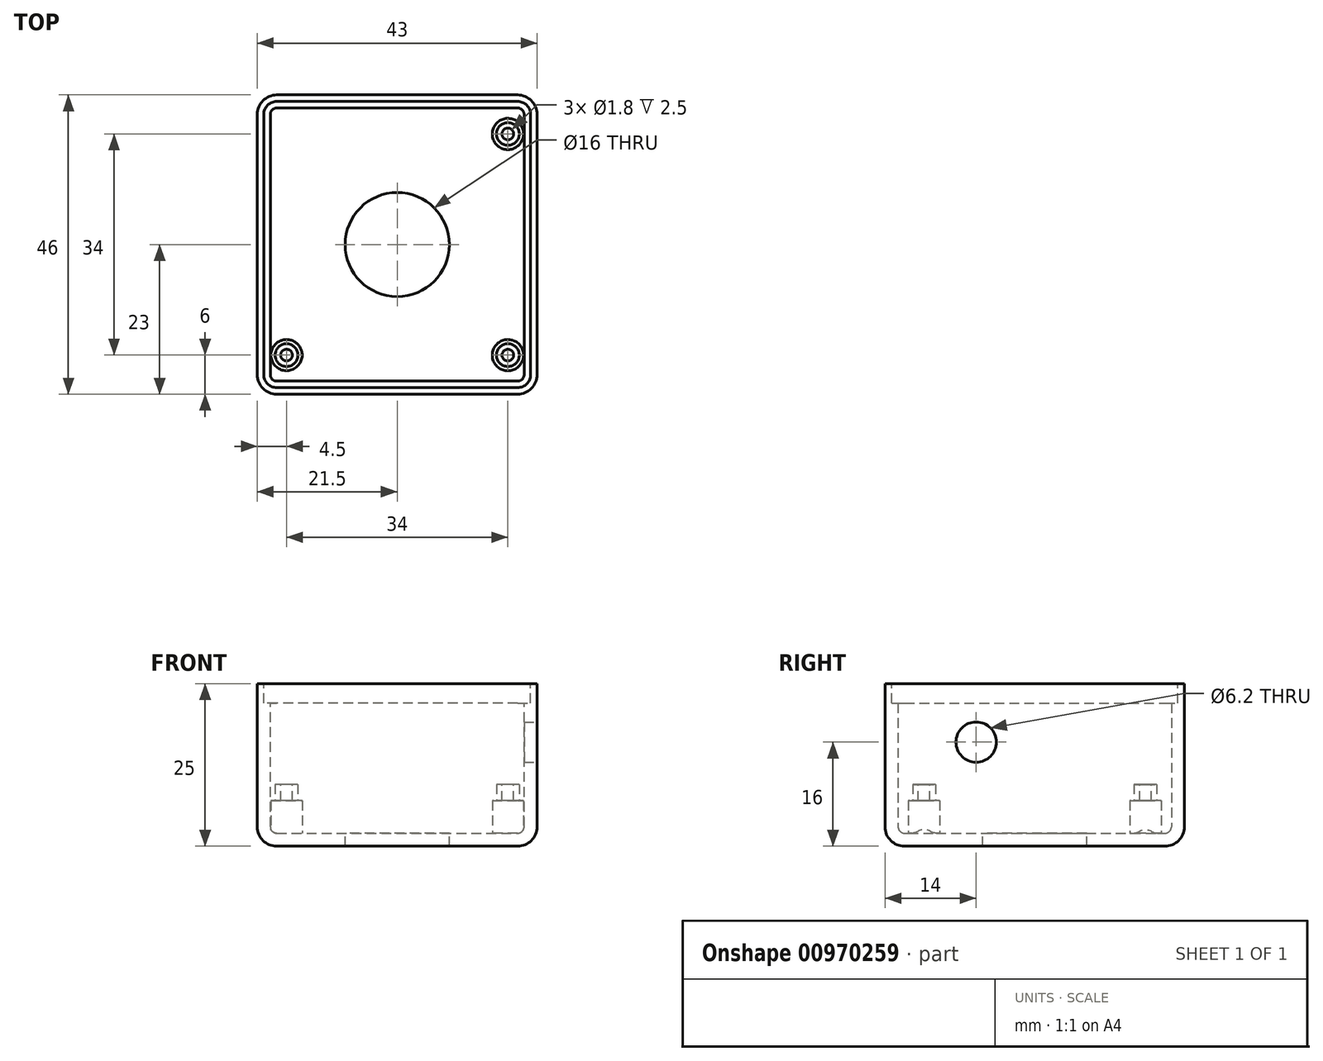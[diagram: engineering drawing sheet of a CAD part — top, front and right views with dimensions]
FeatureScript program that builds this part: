
annotation { "Feature Type Name" : "Feature", "Feature Type Description" : "" }
export const myFeature = defineFeature(function(context is Context, id is Id, definition is map)
    precondition{}
    {
        {
            var Q0;
            Q0=qCreatedBy(makeId("Top.planeOp"),FACE);
            var sketch = newSketch(context, id + "F0", { "sketchPlane" : qUnion([Q0])});
            skLineSegment(sketch, "E0.bottom", {"start": v(21.5, -23) * mm, "end": v(-21.5, -23) * mm});
            skLineSegment(sketch, "E0.top", {"start": v(21.5, 23) * mm, "end": v(-21.5, 23) * mm});
            skLineSegment(sketch, "E0.left", {"start": v(21.5, -23) * mm, "end": v(21.5, 23) * mm});
            skLineSegment(sketch, "E0.right", {"start": v(-21.5, -23) * mm, "end": v(-21.5, 23) * mm});
            skPoint(sketch, "E0.middle", {"position": v(0, 0) * mm});
            skSolve(sketch);
        }
        {
            var Q0;
            Q0=makeQuery(id+"F0.imprint","IMPRINT",FACE,{"disambiguationData":[TD([[makeQuery(id+"F0.imprint","IMPRINT",EDGE,{"derivedFrom":sQuery(id+"F0.wireOp",EDGE,"E0.bottom")}),-1.0]])]});
            extrude(context, id + "F1", {"entities" : qUnion([Q0]), "depth" : 25 * mm, "offsetDistance" : 25 * mm});
        }
        {
            var Q0;
            Q0=makeQuery(id+"F1.opExtrude","CAP_EDGE",EDGE,{"disambiguationData":[OSD([sQuery(id+"F0.wireOp",EDGE,"E0.left")])],"isStart":true});
            var Q1;
            Q1=makeQuery(id+"F1.opExtrude","CAP_FACE",FACE,{"disambiguationData":[OSD([sQuery(id+"F0.wireOp",EDGE,"E0.bottom"),sQuery(id+"F0.wireOp",EDGE,"E0.top"),sQuery(id+"F0.wireOp",EDGE,"E0.left"),sQuery(id+"F0.wireOp",EDGE,"E0.right")])],"isStart":true});
            var Q2;
            Q2=makeQuery(id+"F1.opExtrude","SWEPT_EDGE",EDGE,{"disambiguationData":[OSD([sQuery(id+"F0.wireOp",EDGE,"E0.top"),sQuery(id+"F0.wireOp",EDGE,"E0.left")])]});
            var Q3;
            Q3=makeQuery(id+"F1.opExtrude","SWEPT_EDGE",EDGE,{"disambiguationData":[OSD([sQuery(id+"F0.wireOp",EDGE,"E0.bottom"),sQuery(id+"F0.wireOp",EDGE,"E0.left")])]});
            var Q4;
            Q4=makeQuery(id+"F1.opExtrude","SWEPT_EDGE",EDGE,{"disambiguationData":[OSD([sQuery(id+"F0.wireOp",EDGE,"E0.bottom"),sQuery(id+"F0.wireOp",EDGE,"E0.right")])]});
            var Q5;
            Q5=makeQuery(id+"F1.opExtrude","SWEPT_EDGE",EDGE,{"disambiguationData":[OSD([sQuery(id+"F0.wireOp",EDGE,"E0.top"),sQuery(id+"F0.wireOp",EDGE,"E0.right")])]});
            fillet(context, id + "F2", {"entities" : qUnion([Q0, Q1, Q2, Q3, Q4, Q5]), "radius" : 3 * mm, "tangentPropagation" : true, "allowEdgeOverflow" : false});
        }
        {
            var Q0;
            Q0=makeQuery(id+"F1.opExtrude","CAP_FACE",FACE,{"disambiguationData":[OSD([sQuery(id+"F0.wireOp",EDGE,"E0.bottom"),sQuery(id+"F0.wireOp",EDGE,"E0.top"),sQuery(id+"F0.wireOp",EDGE,"E0.left"),sQuery(id+"F0.wireOp",EDGE,"E0.right")])],"isStart":false});
            shell(context, id + "F3", {"entities" : qUnion([Q0]), "thickness" : 2 * mm});
        }
        {
            var Q0;
            Q0=makeQuery(id+"F3.opShell","OFFSET_FACE",FACE,{"disambiguationData":[OSD([sQuery(id+"F0.wireOp",EDGE,"E0.bottom"),sQuery(id+"F0.wireOp",EDGE,"E0.top"),sQuery(id+"F0.wireOp",EDGE,"E0.left"),sQuery(id+"F0.wireOp",EDGE,"E0.right")])]});
            var sketch = newSketch(context, id + "F4", { "sketchPlane" : qUnion([Q0])});
            skCircle(sketch, "E1", {"center": v(0, 0) * mm, "radius": 8 * mm});
            skSolve(sketch);
        }
        {
            var Q0;
            Q0=qSketchRegion(id+"F4",true);
            extrude(context, id + "F5", {"entities" : qUnion([Q0]), "operationType" : NewBodyOperationType.REMOVE, "endBound" : BoundingType.UP_TO_NEXT, "oppositeDirection" : true, "depth" : 25 * mm, "offsetDistance" : 25 * mm});
        }
        {
            var Q0;
            Q0=makeQuery(id+"F1.opExtrude","SWEPT_FACE",FACE,{"disambiguationData":[OSD([sQuery(id+"F0.wireOp",EDGE,"E0.left")])]});
            var sketch = newSketch(context, id + "F6", { "sketchPlane" : qUnion([Q0])});
            skCircle(sketch, "E2", {"center": v(-9, 16) * mm, "radius": 3.1 * mm});
            skSolve(sketch);
        }
        {
            var Q0;
            Q0=qSketchRegion(id+"F6",true);
            extrude(context, id + "F7", {"entities" : qUnion([Q0]), "operationType" : NewBodyOperationType.REMOVE, "endBound" : BoundingType.UP_TO_NEXT, "oppositeDirection" : true, "depth" : 25 * mm, "offsetDistance" : 25 * mm});
        }
        {
            var Q0;
            Q0=makeQuery(id+"F3.opShell","OFFSET_FACE",FACE,{"disambiguationData":[OSD([sQuery(id+"F0.wireOp",EDGE,"E0.bottom"),sQuery(id+"F0.wireOp",EDGE,"E0.top"),sQuery(id+"F0.wireOp",EDGE,"E0.left"),sQuery(id+"F0.wireOp",EDGE,"E0.right")])]});
            var sketch = newSketch(context, id + "F8", { "sketchPlane" : qUnion([Q0])});
            skCircle(sketch, "E3", {"center": v(17, 17) * mm, "radius": 1.75 * mm});
            skCircle(sketch, "E4", {"center": v(17, -17) * mm, "radius": 1.75 * mm});
            skCircle(sketch, "E5", {"center": v(-17, -17) * mm, "radius": 1.75 * mm});
            skSolve(sketch);
        }
        {
            var Q0;
            Q0=qSketchRegion(id+"F8",true);
            extrude(context, id + "F9", {"entities" : qUnion([Q0]), "operationType" : NewBodyOperationType.ADD, "depth" : 7.5 * mm, "offsetDistance" : 25 * mm});
        }
        {
            var Q0;
            Q0=makeQuery(id+"F3.opShell","OFFSET_FACE",FACE,{"disambiguationData":[OSD([sQuery(id+"F0.wireOp",EDGE,"E0.bottom"),sQuery(id+"F0.wireOp",EDGE,"E0.top"),sQuery(id+"F0.wireOp",EDGE,"E0.left"),sQuery(id+"F0.wireOp",EDGE,"E0.right")])]});
            cPlane(context, id + "F10", {"entities" : qUnion([Q0]), "cplaneType" : CPlaneType.OFFSET, "offset" : 7.5 * mm, "width" : 150 * mm, "height" : 150 * mm});
        }
        {
            var Q0;
            Q0=qCreatedBy(id+"F10.planeOp",FACE);
            var sketch = newSketch(context, id + "F11", { "sketchPlane" : qUnion([Q0])});
            skCircle(sketch, "E6", {"center": v(17, 17) * mm, "radius": 0.9 * mm});
            skCircle(sketch, "E7", {"center": v(17, -17) * mm, "radius": 0.9 * mm});
            skCircle(sketch, "E8", {"center": v(-17, -17) * mm, "radius": 0.9 * mm});
            skSolve(sketch);
        }
        {
            var Q0;
            Q0=qSketchRegion(id+"F11",true);
            extrude(context, id + "F12", {"entities" : qUnion([Q0]), "operationType" : NewBodyOperationType.REMOVE, "oppositeDirection" : true, "depth" : 7 * mm, "offsetDistance" : 25 * mm});
        }
        {
            var Q0;
            Q0=makeQuery(id+"F1.opExtrude","CAP_FACE",FACE,{"disambiguationData":[OSD([sQuery(id+"F0.wireOp",EDGE,"E0.bottom"),sQuery(id+"F0.wireOp",EDGE,"E0.top"),sQuery(id+"F0.wireOp",EDGE,"E0.left"),sQuery(id+"F0.wireOp",EDGE,"E0.right")])],"isStart":false});
            cPlane(context, id + "F13", {"entities" : qUnion([Q0]), "cplaneType" : CPlaneType.OFFSET, "offset" : 0 * mm, "width" : 150 * mm, "height" : 150 * mm});
        }
        {
            var Q0;
            Q0=qCreatedBy(id+"F13.planeOp",FACE);
            var sketch = newSketch(context, id + "F14", { "sketchPlane" : qUnion([Q0])});
            skLineSegment(sketch, "E9.0", {"start": v(18.5, -22) * mm, "end": v(-18.5, -22) * mm});
            skArc(sketch, "E10.0", {"start": v(18.5, -22) * mm, "mid": v(19.91, -21.41) * mm, "end": v(20.5, -20) * mm});
            skLineSegment(sketch, "E11.0", {"start": v(20.5, -20) * mm, "end": v(20.5, 20) * mm});
            skArc(sketch, "E12.0", {"start": v(20.5, 20) * mm, "mid": v(19.91, 21.41) * mm, "end": v(18.5, 22) * mm});
            skLineSegment(sketch, "E13.0", {"start": v(18.5, 22) * mm, "end": v(-18.5, 22) * mm});
            skArc(sketch, "E14.0", {"start": v(-18.5, 22) * mm, "mid": v(-19.91, 21.41) * mm, "end": v(-20.5, 20) * mm});
            skLineSegment(sketch, "E15.0", {"start": v(-20.5, -20) * mm, "end": v(-20.5, 20) * mm});
            skArc(sketch, "E16.0", {"start": v(-20.5, -20) * mm, "mid": v(-19.91, -21.41) * mm, "end": v(-18.5, -22) * mm});
            skSolve(sketch);
        }
        {
            var Q0;
            Q0=qSketchRegion(id+"F14",true);
            extrude(context, id + "F15", {"entities" : qUnion([Q0]), "operationType" : NewBodyOperationType.REMOVE, "oppositeDirection" : true, "depth" : 3 * mm, "offsetDistance" : 25 * mm});
        }
        {
            var Q0;
            Q0=makeQuery(id+"F3.opShell","OFFSET_FACE",FACE,{"disambiguationData":[OSD([sQuery(id+"F0.wireOp",EDGE,"E0.bottom"),sQuery(id+"F0.wireOp",EDGE,"E0.top"),sQuery(id+"F0.wireOp",EDGE,"E0.left"),sQuery(id+"F0.wireOp",EDGE,"E0.right")])]});
            var sketch = newSketch(context, id + "F16", { "sketchPlane" : qUnion([Q0])});
            skCircle(sketch, "E17", {"center": v(17, 17) * mm, "radius": 2.4 * mm});
            skCircle(sketch, "E18", {"center": v(17, -17) * mm, "radius": 2.4 * mm});
            skCircle(sketch, "E19", {"center": v(-17, -17) * mm, "radius": 2.4 * mm});
            skSolve(sketch);
        }
        {
            var Q0;
            Q0=qSketchRegion(id+"F16",true);
            extrude(context, id + "F17", {"entities" : qUnion([Q0]), "operationType" : NewBodyOperationType.ADD, "depth" : 5 * mm, "offsetDistance" : 25 * mm});
        }
    });
